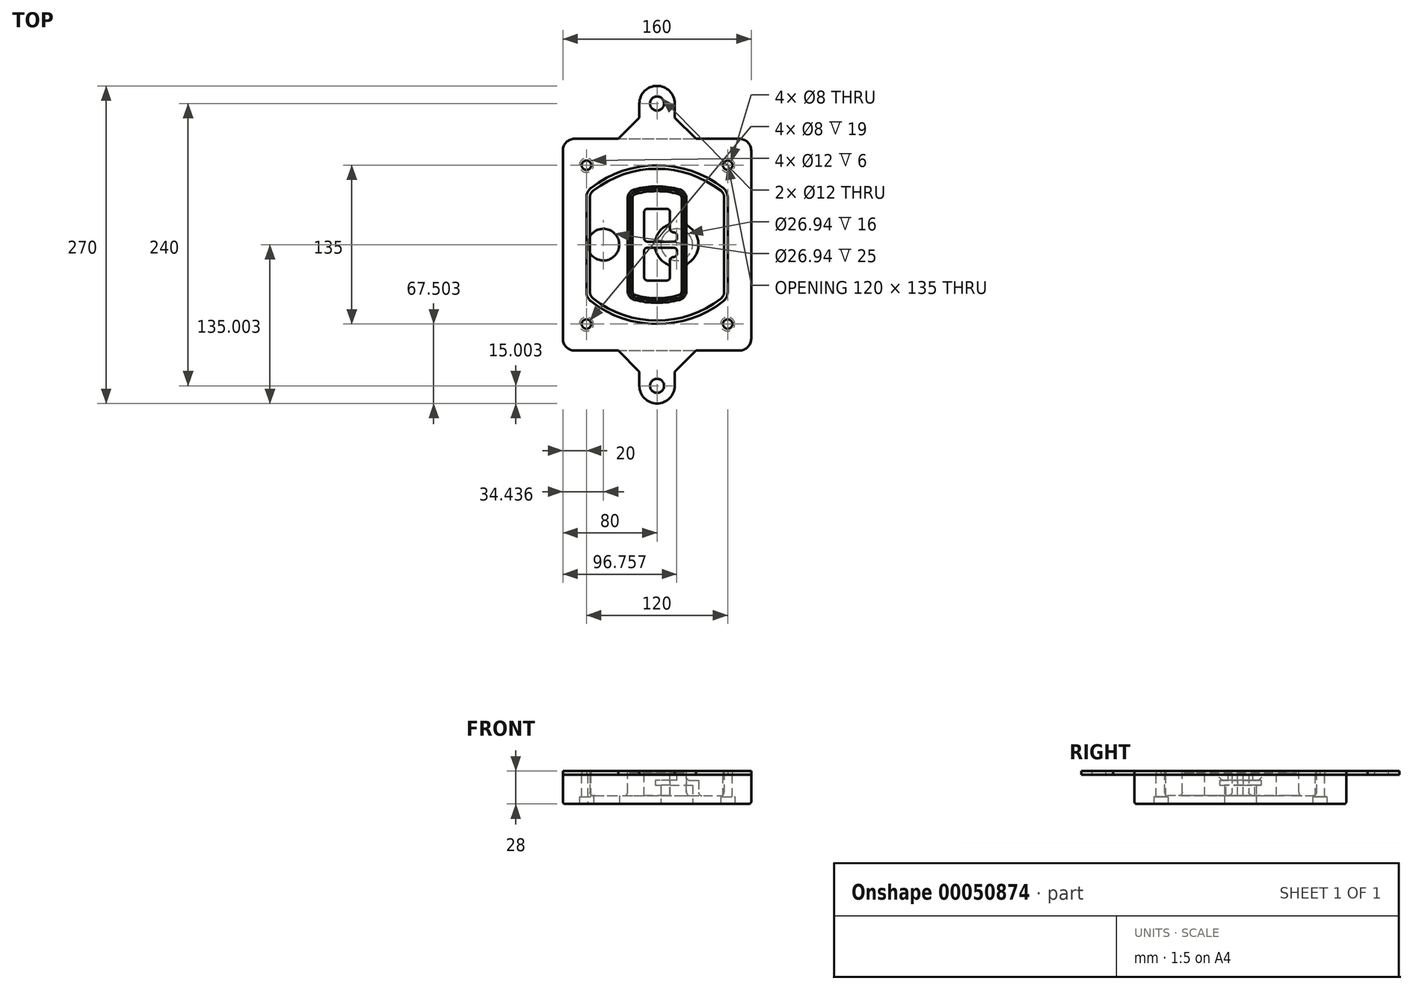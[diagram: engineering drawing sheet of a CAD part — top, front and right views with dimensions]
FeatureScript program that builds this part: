
annotation { "Feature Type Name" : "Feature", "Feature Type Description" : "" }
export const myFeature = defineFeature(function(context is Context, id is Id, definition is map)
    precondition{}
    {
        {
            var Q0;
            Q0=qCreatedBy(makeId("Top.planeOp"),FACE);
            var sketch = newSketch(context, id + "F0", { "sketchPlane" : qUnion([Q0])});
            skPoint(sketch, "E0.rect.middle", {"position": v(0, 0) * mm});
            skLineSegment(sketch, "E1.bottom", {"start": v(24.05, 28.38) * mm, "end": v(164.05, 28.38) * mm});
            skLineSegment(sketch, "E1.top", {"start": v(24.05, 208.38) * mm, "end": v(164.05, 208.38) * mm});
            skLineSegment(sketch, "E1.left", {"start": v(14.05, 38.38) * mm, "end": v(14.05, 198.38) * mm});
            skLineSegment(sketch, "E1.right", {"start": v(174.05, 38.38) * mm, "end": v(174.05, 198.38) * mm});
            skLineSegment(sketch, "E2", {"start": v(14.05, 208.38) * mm, "end": v(174.05, 28.38) * mm, "construction": true});
            skLineSegment(sketch, "E3", {"start": v(174.05, 208.38) * mm, "end": v(14.05, 28.38) * mm, "construction": true});
            skCircle(sketch, "E4", {"center": v(34.05, 185.88) * mm, "radius": 4 * mm});
            skCircle(sketch, "E5", {"center": v(154.05, 185.88) * mm, "radius": 4 * mm});
            skCircle(sketch, "E6", {"center": v(154.05, 50.88) * mm, "radius": 4 * mm});
            skCircle(sketch, "E7", {"center": v(34.05, 50.88) * mm, "radius": 4 * mm});
            skLineSegment(sketch, "E8", {"start": v(34.05, 185.88) * mm, "end": v(154.05, 185.88) * mm, "construction": true});
            skLineSegment(sketch, "E9", {"start": v(154.05, 185.88) * mm, "end": v(154.05, 50.88) * mm, "construction": true});
            skLineSegment(sketch, "E10", {"start": v(154.05, 50.88) * mm, "end": v(34.05, 50.88) * mm, "construction": true});
            skLineSegment(sketch, "E11", {"start": v(34.05, 50.88) * mm, "end": v(34.05, 185.88) * mm, "construction": true});
            skLineSegment(sketch, "E12", {"start": v(34.05, 158.68) * mm, "end": v(34.05, 78.09) * mm});
            skLineSegment(sketch, "E13", {"start": v(154.05, 158.68) * mm, "end": v(154.05, 78.09) * mm});
            skArc(sketch, "E14", {"start": v(150.2, 166.56) * mm, "mid": v(94.05, 185.88) * mm, "end": v(37.9, 166.56) * mm});
            skArc(sketch, "E15", {"start": v(37.9, 70.2) * mm, "mid": v(94.05, 50.88) * mm, "end": v(150.2, 70.2) * mm});
            skLineSegment(sketch, "E16", {"start": v(34.05, 118.38) * mm, "end": v(154.05, 118.38) * mm, "construction": true});
            skPoint(sketch, "E17.visualSharp", {"position": v(34.05, 73.38) * mm});
            skArc(sketch, "E17.filletArc", {"start": v(34.05, 78.09) * mm, "mid": v(35.06, 73.7) * mm, "end": v(37.9, 70.2) * mm});
            skPoint(sketch, "E18.visualSharp", {"position": v(34.05, 163.38) * mm});
            skArc(sketch, "E18.filletArc", {"start": v(37.9, 166.56) * mm, "mid": v(35.06, 163.06) * mm, "end": v(34.05, 158.68) * mm});
            skPoint(sketch, "E19.visualSharp", {"position": v(154.05, 163.38) * mm});
            skArc(sketch, "E19.filletArc", {"start": v(154.05, 158.68) * mm, "mid": v(153.04, 163.06) * mm, "end": v(150.2, 166.56) * mm});
            skPoint(sketch, "E20.visualSharp", {"position": v(154.05, 73.38) * mm});
            skArc(sketch, "E20.filletArc", {"start": v(150.2, 70.2) * mm, "mid": v(153.04, 73.7) * mm, "end": v(154.05, 78.09) * mm});
            skPoint(sketch, "E21.visualSharp", {"position": v(14.05, 208.38) * mm});
            skArc(sketch, "E21.filletArc", {"start": v(24.05, 208.38) * mm, "mid": v(16.98, 205.45) * mm, "end": v(14.05, 198.38) * mm});
            skPoint(sketch, "E22.visualSharp", {"position": v(174.05, 208.38) * mm});
            skArc(sketch, "E22.filletArc", {"start": v(174.05, 198.38) * mm, "mid": v(171.12, 205.45) * mm, "end": v(164.05, 208.38) * mm});
            skPoint(sketch, "E23.visualSharp", {"position": v(174.05, 28.38) * mm});
            skArc(sketch, "E23.filletArc", {"start": v(164.05, 28.38) * mm, "mid": v(171.12, 31.31) * mm, "end": v(174.05, 38.38) * mm});
            skPoint(sketch, "E24.visualSharp", {"position": v(14.05, 28.38) * mm});
            skArc(sketch, "E24.filletArc", {"start": v(14.05, 38.38) * mm, "mid": v(16.98, 31.31) * mm, "end": v(24.05, 28.38) * mm});
            skArc(sketch, "E25.0", {"start": v(151.05, 158.68) * mm, "mid": v(150.34, 161.75) * mm, "end": v(148.36, 164.2) * mm});
            skLineSegment(sketch, "E25.1", {"start": v(151.05, 158.68) * mm, "end": v(151.05, 78.09) * mm});
            skArc(sketch, "E25.2", {"start": v(148.36, 72.57) * mm, "mid": v(150.34, 75.02) * mm, "end": v(151.05, 78.09) * mm});
            skArc(sketch, "E25.3", {"start": v(39.74, 72.57) * mm, "mid": v(94.05, 53.88) * mm, "end": v(148.36, 72.57) * mm});
            skArc(sketch, "E25.4", {"start": v(37.05, 78.09) * mm, "mid": v(37.76, 75.02) * mm, "end": v(39.74, 72.57) * mm});
            skArc(sketch, "E25.5", {"start": v(148.36, 164.2) * mm, "mid": v(94.05, 182.88) * mm, "end": v(39.74, 164.2) * mm});
            skLineSegment(sketch, "E25.6", {"start": v(37.05, 158.68) * mm, "end": v(37.05, 78.09) * mm});
            skArc(sketch, "E25.7", {"start": v(39.74, 164.2) * mm, "mid": v(37.76, 161.75) * mm, "end": v(37.05, 158.68) * mm});
            skArc(sketch, "E26.0", {"start": v(35.43, 169.71) * mm, "mid": v(31.47, 164.82) * mm, "end": v(30.05, 158.68) * mm});
            skArc(sketch, "E26.1", {"start": v(152.67, 169.71) * mm, "mid": v(94.05, 189.88) * mm, "end": v(35.43, 169.71) * mm});
            skArc(sketch, "E26.2", {"start": v(158.05, 158.68) * mm, "mid": v(156.63, 164.82) * mm, "end": v(152.67, 169.71) * mm});
            skLineSegment(sketch, "E26.3", {"start": v(158.05, 158.68) * mm, "end": v(158.05, 78.09) * mm});
            skArc(sketch, "E26.4", {"start": v(152.67, 67.05) * mm, "mid": v(156.63, 71.95) * mm, "end": v(158.05, 78.09) * mm});
            skLineSegment(sketch, "E26.5", {"start": v(30.05, 158.68) * mm, "end": v(30.05, 78.09) * mm});
            skArc(sketch, "E26.6", {"start": v(35.43, 67.05) * mm, "mid": v(94.05, 46.88) * mm, "end": v(152.67, 67.05) * mm});
            skArc(sketch, "E26.7", {"start": v(30.05, 78.09) * mm, "mid": v(31.47, 71.95) * mm, "end": v(35.43, 67.05) * mm});
            skSolve(sketch);
        }
        {
            var Q0;
            Q0=makeQuery(id+"F0.imprint","IMPRINT",FACE,{"disambiguationData":[TD([[makeQuery(id+"F0.imprint","IMPRINT",EDGE,{"derivedFrom":sQuery(id+"F0.wireOp",EDGE,"E1.bottom")}),1.0]])]});
            var Q1;
            Q1=makeQuery(id+"F0.imprint","IMPRINT",FACE,{"disambiguationData":[TD([[makeQuery(id+"F0.imprint","IMPRINT",EDGE,{"derivedFrom":sQuery(id+"F0.wireOp",EDGE,"E12")}),1.0]])]});
            var Q2;
            Q2=makeQuery(id+"F0.imprint","IMPRINT",FACE,{"disambiguationData":[TD([[makeQuery(id+"F0.imprint","IMPRINT",EDGE,{"derivedFrom":sQuery(id+"F0.wireOp",EDGE,"E25.0")}),1.0]])]});
            var Q3;
            Q3=makeQuery(id+"F0.imprint","IMPRINT",FACE,{"disambiguationData":[TD([[makeQuery(id+"F0.imprint","IMPRINT",EDGE,{"derivedFrom":sQuery(id+"F0.wireOp",EDGE,"E12")}),-1.0]])]});
            extrude(context, id + "F1", {"entities" : qUnion([Q0, Q1, Q2, Q3]), "oppositeDirection" : true, "depth" : 25 * mm});
        }
        {
            var Q0;
            Q0=makeQuery(id+"F0.imprint","IMPRINT",FACE,{"disambiguationData":[TD([[makeQuery(id+"F0.imprint","IMPRINT",EDGE,{"derivedFrom":sQuery(id+"F0.wireOp",EDGE,"E12")}),1.0]])]});
            extrude(context, id + "F2", {"entities" : qUnion([Q0]), "operationType" : NewBodyOperationType.ADD, "depth" : 3 * mm});
        }
        {
            var Q0;
            Q0=makeQuery(id+"F0.imprint","IMPRINT",FACE,{"disambiguationData":[TD([[makeQuery(id+"F0.imprint","IMPRINT",EDGE,{"derivedFrom":sQuery(id+"F0.wireOp",EDGE,"E25.0")}),1.0]])]});
            extrude(context, id + "F3", {"entities" : qUnion([Q0]), "operationType" : NewBodyOperationType.REMOVE, "oppositeDirection" : true, "depth" : 18 * mm});
        }
        {
            var Q0;
            Q0=makeQuery(id+"F2.opExtrude","CAP_FACE",FACE,{"disambiguationData":[OSD([sQuery(id+"F0.wireOp",EDGE,"E12"),sQuery(id+"F0.wireOp",EDGE,"E13"),sQuery(id+"F0.wireOp",EDGE,"E14"),sQuery(id+"F0.wireOp",EDGE,"E15"),sQuery(id+"F0.wireOp",EDGE,"E17.filletArc"),sQuery(id+"F0.wireOp",EDGE,"E18.filletArc"),sQuery(id+"F0.wireOp",EDGE,"E19.filletArc"),sQuery(id+"F0.wireOp",EDGE,"E20.filletArc"),sQuery(id+"F0.wireOp",EDGE,"E25.0"),sQuery(id+"F0.wireOp",EDGE,"E25.1"),sQuery(id+"F0.wireOp",EDGE,"E25.2"),sQuery(id+"F0.wireOp",EDGE,"E25.3"),sQuery(id+"F0.wireOp",EDGE,"E25.4"),sQuery(id+"F0.wireOp",EDGE,"E25.5"),sQuery(id+"F0.wireOp",EDGE,"E25.6"),sQuery(id+"F0.wireOp",EDGE,"E25.7")])],"isStart":false});
            var sketch = newSketch(context, id + "F4", { "sketchPlane" : qUnion([Q0])});
            skArc(sketch, "E27.0", {"start": v(74.97, 71.41) * mm, "mid": v(94.05, 68.88) * mm, "end": v(113.13, 71.41) * mm});
            skArc(sketch, "E28.0", {"start": v(113.13, 165.35) * mm, "mid": v(94.05, 167.88) * mm, "end": v(74.97, 165.35) * mm});
            skLineSegment(sketch, "E29", {"start": v(69.05, 157.63) * mm, "end": v(69.05, 79.14) * mm});
            skLineSegment(sketch, "E30", {"start": v(119.05, 157.63) * mm, "end": v(119.05, 79.14) * mm});
            skLineSegment(sketch, "E31", {"start": v(69.05, 163.48) * mm, "end": v(119.05, 163.48) * mm, "construction": true});
            skLineSegment(sketch, "E32", {"start": v(69.05, 73.28) * mm, "end": v(119.05, 73.28) * mm, "construction": true});
            skPoint(sketch, "E33.visualSharp", {"position": v(69.05, 163.48) * mm});
            skArc(sketch, "E33.filletArc", {"start": v(74.97, 165.35) * mm, "mid": v(70.7, 162.5) * mm, "end": v(69.05, 157.63) * mm});
            skPoint(sketch, "E34.visualSharp", {"position": v(119.05, 163.48) * mm});
            skArc(sketch, "E34.filletArc", {"start": v(119.05, 157.63) * mm, "mid": v(117.4, 162.5) * mm, "end": v(113.13, 165.35) * mm});
            skPoint(sketch, "E35.visualSharp", {"position": v(119.05, 73.28) * mm});
            skArc(sketch, "E35.filletArc", {"start": v(113.13, 71.41) * mm, "mid": v(117.4, 74.27) * mm, "end": v(119.05, 79.14) * mm});
            skPoint(sketch, "E36.visualSharp", {"position": v(69.05, 73.28) * mm});
            skArc(sketch, "E36.filletArc", {"start": v(69.05, 79.14) * mm, "mid": v(70.7, 74.27) * mm, "end": v(74.97, 71.41) * mm});
            skArc(sketch, "E37.0", {"start": v(148.36, 164.2) * mm, "mid": v(94.05, 182.88) * mm, "end": v(39.74, 164.2) * mm});
            skArc(sketch, "E37.1", {"start": v(39.74, 164.2) * mm, "mid": v(37.76, 161.75) * mm, "end": v(37.05, 158.68) * mm});
            skLineSegment(sketch, "E37.2", {"start": v(37.05, 158.68) * mm, "end": v(37.05, 78.09) * mm});
            skArc(sketch, "E37.3", {"start": v(37.05, 78.09) * mm, "mid": v(37.76, 75.02) * mm, "end": v(39.74, 72.57) * mm});
            skArc(sketch, "E37.4", {"start": v(39.74, 72.57) * mm, "mid": v(94.05, 53.88) * mm, "end": v(148.36, 72.57) * mm});
            skArc(sketch, "E37.5", {"start": v(148.36, 72.57) * mm, "mid": v(150.34, 75.02) * mm, "end": v(151.05, 78.09) * mm});
            skLineSegment(sketch, "E37.6", {"start": v(151.05, 158.68) * mm, "end": v(151.05, 78.09) * mm});
            skArc(sketch, "E37.7", {"start": v(151.05, 158.68) * mm, "mid": v(150.34, 161.75) * mm, "end": v(148.36, 164.2) * mm});
            skLineSegment(sketch, "E38.0", {"start": v(117.05, 157.63) * mm, "end": v(117.05, 79.14) * mm});
            skArc(sketch, "E38.1", {"start": v(112.61, 73.34) * mm, "mid": v(115.81, 75.49) * mm, "end": v(117.05, 79.14) * mm});
            skArc(sketch, "E38.2", {"start": v(75.49, 73.34) * mm, "mid": v(94.05, 70.88) * mm, "end": v(112.61, 73.34) * mm});
            skArc(sketch, "E38.3", {"start": v(71.05, 79.14) * mm, "mid": v(72.29, 75.49) * mm, "end": v(75.49, 73.34) * mm});
            skLineSegment(sketch, "E38.4", {"start": v(71.05, 157.63) * mm, "end": v(71.05, 79.14) * mm});
            skArc(sketch, "E38.5", {"start": v(117.05, 157.63) * mm, "mid": v(115.81, 161.28) * mm, "end": v(112.61, 163.42) * mm});
            skArc(sketch, "E38.6", {"start": v(75.49, 163.42) * mm, "mid": v(72.29, 161.28) * mm, "end": v(71.05, 157.63) * mm});
            skArc(sketch, "E38.7", {"start": v(112.61, 163.42) * mm, "mid": v(94.05, 165.88) * mm, "end": v(75.49, 163.42) * mm});
            skArc(sketch, "E39.0", {"start": v(115.05, 157.63) * mm, "mid": v(114.23, 160.06) * mm, "end": v(112.1, 161.5) * mm});
            skLineSegment(sketch, "E39.1", {"start": v(115.05, 157.63) * mm, "end": v(115.05, 79.14) * mm});
            skArc(sketch, "E39.2", {"start": v(112.1, 75.27) * mm, "mid": v(114.23, 76.7) * mm, "end": v(115.05, 79.14) * mm});
            skArc(sketch, "E39.3", {"start": v(76, 75.27) * mm, "mid": v(94.05, 72.88) * mm, "end": v(112.1, 75.27) * mm});
            skArc(sketch, "E39.4", {"start": v(73.05, 79.14) * mm, "mid": v(73.87, 76.7) * mm, "end": v(76, 75.27) * mm});
            skArc(sketch, "E39.5", {"start": v(112.1, 161.5) * mm, "mid": v(94.05, 163.88) * mm, "end": v(76, 161.5) * mm});
            skLineSegment(sketch, "E39.6", {"start": v(73.05, 157.63) * mm, "end": v(73.05, 79.14) * mm});
            skArc(sketch, "E39.7", {"start": v(76, 161.5) * mm, "mid": v(73.87, 160.06) * mm, "end": v(73.05, 157.63) * mm});
            skLineSegment(sketch, "E40", {"start": v(69.05, 118.38) * mm, "end": v(119.05, 118.38) * mm, "construction": true});
            skLineSegment(sketch, "E41", {"start": v(83.05, 123.88) * mm, "end": v(83.05, 145.88) * mm});
            skLineSegment(sketch, "E42", {"start": v(86.05, 148.88) * mm, "end": v(102.05, 148.88) * mm});
            skLineSegment(sketch, "E43", {"start": v(105.05, 145.88) * mm, "end": v(105.05, 131.88) * mm});
            skLineSegment(sketch, "E44", {"start": v(108.05, 128.88) * mm, "end": v(108.05, 128.88) * mm});
            skLineSegment(sketch, "E45", {"start": v(111.05, 125.88) * mm, "end": v(111.05, 123.88) * mm});
            skLineSegment(sketch, "E46", {"start": v(108.05, 120.88) * mm, "end": v(86.05, 120.88) * mm});
            skPoint(sketch, "E47.visualSharp", {"position": v(83.05, 148.88) * mm});
            skArc(sketch, "E47.filletArc", {"start": v(86.05, 148.88) * mm, "mid": v(83.93, 148) * mm, "end": v(83.05, 145.88) * mm});
            skPoint(sketch, "E48.visualSharp", {"position": v(105.05, 148.88) * mm});
            skArc(sketch, "E48.filletArc", {"start": v(105.05, 145.88) * mm, "mid": v(104.17, 148) * mm, "end": v(102.05, 148.88) * mm});
            skPoint(sketch, "E49.visualSharp", {"position": v(105.05, 128.88) * mm});
            skArc(sketch, "E49.filletArc", {"start": v(105.05, 131.88) * mm, "mid": v(105.93, 129.76) * mm, "end": v(108.05, 128.88) * mm});
            skPoint(sketch, "E50.visualSharp", {"position": v(111.05, 128.88) * mm});
            skArc(sketch, "E50.filletArc", {"start": v(111.05, 125.88) * mm, "mid": v(110.17, 128) * mm, "end": v(108.05, 128.88) * mm});
            skPoint(sketch, "E51.visualSharp", {"position": v(111.05, 120.88) * mm});
            skArc(sketch, "E51.filletArc", {"start": v(108.05, 120.88) * mm, "mid": v(110.17, 121.76) * mm, "end": v(111.05, 123.88) * mm});
            skPoint(sketch, "E52.visualSharp", {"position": v(83.05, 120.88) * mm});
            skArc(sketch, "E52.filletArc", {"start": v(83.05, 123.88) * mm, "mid": v(83.93, 121.76) * mm, "end": v(86.05, 120.88) * mm});
            skLineSegment(sketch, "E53.0.MirrorCS", {"start": v(108.05, 115.88) * mm, "end": v(86.05, 115.88) * mm});
            skArc(sketch, "E54.0.MirrorCS", {"start": v(83.05, 112.88) * mm, "mid": v(83.93, 115) * mm, "end": v(86.05, 115.88) * mm});
            skLineSegment(sketch, "E55.0.MirrorCS", {"start": v(83.05, 112.88) * mm, "end": v(83.05, 90.88) * mm});
            skArc(sketch, "E56.0.MirrorCS", {"start": v(86.05, 87.88) * mm, "mid": v(83.93, 88.76) * mm, "end": v(83.05, 90.88) * mm});
            skLineSegment(sketch, "E57.0.MirrorCS", {"start": v(86.05, 87.88) * mm, "end": v(102.05, 87.88) * mm});
            skArc(sketch, "E58.0.MirrorCS", {"start": v(105.05, 90.88) * mm, "mid": v(104.17, 88.76) * mm, "end": v(102.05, 87.88) * mm});
            skLineSegment(sketch, "E59.0.MirrorCS", {"start": v(105.05, 90.88) * mm, "end": v(105.05, 104.88) * mm});
            skArc(sketch, "E60.0.MirrorCS", {"start": v(105.05, 104.88) * mm, "mid": v(105.93, 107) * mm, "end": v(108.05, 107.88) * mm});
            skArc(sketch, "E61.0.MirrorCS", {"start": v(111.05, 110.88) * mm, "mid": v(110.17, 108.76) * mm, "end": v(108.05, 107.88) * mm});
            skLineSegment(sketch, "E62.0.MirrorCS", {"start": v(111.05, 110.88) * mm, "end": v(111.05, 112.88) * mm});
            skArc(sketch, "E63.0.MirrorCS", {"start": v(108.05, 115.88) * mm, "mid": v(110.17, 115) * mm, "end": v(111.05, 112.88) * mm});
            skSolve(sketch);
        }
        {
            var Q0;
            Q0=makeQuery(id+"F4.imprint","IMPRINT",FACE,{"disambiguationData":[TD([[makeQuery(id+"F4.imprint","IMPRINT",EDGE,{"derivedFrom":sQuery(id+"F4.wireOp",EDGE,"E27.0")}),1.0]])]});
            var Q1;
            Q1=makeQuery(id+"F4.imprint","IMPRINT",FACE,{"disambiguationData":[TD([[makeQuery(id+"F4.imprint","IMPRINT",EDGE,{"derivedFrom":sQuery(id+"F4.wireOp",EDGE,"E38.0")}),-1.0]])]});
            var Q2;
            Q2=makeQuery(id+"F4.imprint","IMPRINT",FACE,{"disambiguationData":[TD([[makeQuery(id+"F4.imprint","IMPRINT",EDGE,{"derivedFrom":sQuery(id+"F4.wireOp",EDGE,"E39.0")}),1.0]])]});
            extrude(context, id + "F5", {"entities" : qUnion([Q0, Q1, Q2]), "operationType" : NewBodyOperationType.ADD, "endBound" : BoundingType.UP_TO_NEXT, "oppositeDirection" : true, "depth" : 25 * mm});
        }
        {
            var Q0;
            Q0=makeQuery(id+"F4.imprint","IMPRINT",FACE,{"disambiguationData":[TD([[makeQuery(id+"F4.imprint","IMPRINT",EDGE,{"derivedFrom":sQuery(id+"F4.wireOp",EDGE,"E38.0")}),-1.0]])]});
            extrude(context, id + "F6", {"entities" : qUnion([Q0]), "operationType" : NewBodyOperationType.REMOVE, "oppositeDirection" : true, "depth" : 2 * mm});
        }
        {
            var Q0;
            Q0=makeQuery(id+"F1.opExtrude","CAP_FACE",FACE,{"disambiguationData":[OSD([sQuery(id+"F0.wireOp",EDGE,"E1.bottom"),sQuery(id+"F0.wireOp",EDGE,"E1.top"),sQuery(id+"F0.wireOp",EDGE,"E1.left"),sQuery(id+"F0.wireOp",EDGE,"E1.right"),sQuery(id+"F0.wireOp",EDGE,"E4"),sQuery(id+"F0.wireOp",EDGE,"E5"),sQuery(id+"F0.wireOp",EDGE,"E6"),sQuery(id+"F0.wireOp",EDGE,"E7"),sQuery(id+"F0.wireOp",EDGE,"E21.filletArc"),sQuery(id+"F0.wireOp",EDGE,"E22.filletArc"),sQuery(id+"F0.wireOp",EDGE,"E23.filletArc"),sQuery(id+"F0.wireOp",EDGE,"E24.filletArc")])],"isStart":false});
            var sketch = newSketch(context, id + "F7", { "sketchPlane" : qUnion([Q0])});
            skCircle(sketch, "E64", {"center": v(110.8, -118.38) * mm, "radius": 13.47 * mm});
            skCircle(sketch, "E65", {"center": v(48.49, -118.38) * mm, "radius": 13.47 * mm});
            skLineSegment(sketch, "E66", {"start": v(174.05, -118.38) * mm, "end": v(14.05, -118.38) * mm});
            skCircle(sketch, "E67", {"center": v(110.8, -118.38) * mm, "radius": 18.47 * mm});
            skCircle(sketch, "E68", {"center": v(154.05, -185.88) * mm, "radius": 6 * mm});
            skCircle(sketch, "E69", {"center": v(34.05, -185.88) * mm, "radius": 6 * mm});
            skCircle(sketch, "E70", {"center": v(34.05, -50.88) * mm, "radius": 6 * mm});
            skCircle(sketch, "E71", {"center": v(154.05, -50.88) * mm, "radius": 6 * mm});
            skSolve(sketch);
        }
        {
            var Q0;
            {var subQ1=sQuery(id+"F7.wireOp",EDGE,"E66");var subQ4=sQuery(id+"F7.wireOp",EDGE,"E64");var subQ6=makeQuery(id+"F7.imprint","INTERSECT",VERTEX,{"disambiguationData":[OD(0.0)],"derivedFrom":[subQ4,subQ1]});Q0=makeQuery(id+"F7.imprint","IMPRINT",FACE,{"disambiguationData":[TD([[makeQuery(id+"F7.imprint","IMPRINT",EDGE,{"disambiguationData":[TD([[subQ6,-1.0]])],"derivedFrom":subQ4}),-1.0]])]});}
            var Q1;
            {var subQ0=sQuery(id+"F7.wireOp",EDGE,"E66");var subQ1=sQuery(id+"F7.wireOp",EDGE,"E64");var subQ3=makeQuery(id+"F7.imprint","INTERSECT",VERTEX,{"disambiguationData":[OD(0.0)],"derivedFrom":[subQ1,subQ0]});Q1=makeQuery(id+"F7.imprint","IMPRINT",FACE,{"disambiguationData":[TD([[makeQuery(id+"F7.imprint","IMPRINT",EDGE,{"disambiguationData":[TD([[subQ3,-1.0]])],"derivedFrom":subQ1}),1.0]])]});}
            var Q2;
            {var subQ0=sQuery(id+"F7.wireOp",EDGE,"E66");var subQ1=sQuery(id+"F7.wireOp",EDGE,"E64");var subQ3=makeQuery(id+"F7.imprint","INTERSECT",VERTEX,{"disambiguationData":[OD(0.0)],"derivedFrom":[subQ1,subQ0]});Q2=makeQuery(id+"F7.imprint","IMPRINT",FACE,{"disambiguationData":[TD([[makeQuery(id+"F7.imprint","IMPRINT",EDGE,{"disambiguationData":[TD([[subQ3,1.0]])],"derivedFrom":subQ1}),1.0]])]});}
            var Q3;
            {var subQ1=sQuery(id+"F7.wireOp",EDGE,"E66");var subQ4=sQuery(id+"F7.wireOp",EDGE,"E64");var subQ6=makeQuery(id+"F7.imprint","INTERSECT",VERTEX,{"disambiguationData":[OD(0.0)],"derivedFrom":[subQ4,subQ1]});Q3=makeQuery(id+"F7.imprint","IMPRINT",FACE,{"disambiguationData":[TD([[makeQuery(id+"F7.imprint","IMPRINT",EDGE,{"disambiguationData":[TD([[subQ6,1.0]])],"derivedFrom":subQ4}),-1.0]])]});}
            extrude(context, id + "F8", {"entities" : qUnion([Q0, Q1, Q2, Q3]), "operationType" : NewBodyOperationType.ADD, "oppositeDirection" : true, "depth" : 20 * mm});
        }
        {
            var Q0;
            {var subQ0=sQuery(id+"F7.wireOp",EDGE,"E66");var subQ1=sQuery(id+"F7.wireOp",EDGE,"E64");var subQ3=makeQuery(id+"F7.imprint","INTERSECT",VERTEX,{"disambiguationData":[OD(0.0)],"derivedFrom":[subQ1,subQ0]});Q0=makeQuery(id+"F7.imprint","IMPRINT",FACE,{"disambiguationData":[TD([[makeQuery(id+"F7.imprint","IMPRINT",EDGE,{"disambiguationData":[TD([[subQ3,-1.0]])],"derivedFrom":subQ1}),1.0]])]});}
            var Q1;
            {var subQ0=sQuery(id+"F7.wireOp",EDGE,"E66");var subQ1=sQuery(id+"F7.wireOp",EDGE,"E64");var subQ3=makeQuery(id+"F7.imprint","INTERSECT",VERTEX,{"disambiguationData":[OD(0.0)],"derivedFrom":[subQ1,subQ0]});Q1=makeQuery(id+"F7.imprint","IMPRINT",FACE,{"disambiguationData":[TD([[makeQuery(id+"F7.imprint","IMPRINT",EDGE,{"disambiguationData":[TD([[subQ3,1.0]])],"derivedFrom":subQ1}),1.0]])]});}
            extrude(context, id + "F9", {"entities" : qUnion([Q0, Q1]), "operationType" : NewBodyOperationType.REMOVE, "oppositeDirection" : true, "depth" : 16 * mm});
        }
        {
            var Q0;
            {var subQ0=sQuery(id+"F7.wireOp",EDGE,"E66");var subQ1=sQuery(id+"F7.wireOp",EDGE,"E65");var subQ3=makeQuery(id+"F7.imprint","INTERSECT",VERTEX,{"disambiguationData":[OD(0.0)],"derivedFrom":[subQ1,subQ0]});Q0=makeQuery(id+"F7.imprint","IMPRINT",FACE,{"disambiguationData":[TD([[makeQuery(id+"F7.imprint","IMPRINT",EDGE,{"disambiguationData":[TD([[subQ3,-1.0]])],"derivedFrom":subQ1}),1.0]])]});}
            var Q1;
            {var subQ0=sQuery(id+"F7.wireOp",EDGE,"E66");var subQ1=sQuery(id+"F7.wireOp",EDGE,"E65");var subQ3=makeQuery(id+"F7.imprint","INTERSECT",VERTEX,{"disambiguationData":[OD(0.0)],"derivedFrom":[subQ1,subQ0]});Q1=makeQuery(id+"F7.imprint","IMPRINT",FACE,{"disambiguationData":[TD([[makeQuery(id+"F7.imprint","IMPRINT",EDGE,{"disambiguationData":[TD([[subQ3,1.0]])],"derivedFrom":subQ1}),1.0]])]});}
            extrude(context, id + "F10", {"entities" : qUnion([Q0, Q1]), "operationType" : NewBodyOperationType.REMOVE, "oppositeDirection" : true, "depth" : 25 * mm});
        }
        {
            var Q0;
            Q0=makeQuery(id+"F7.imprint","IMPRINT",FACE,{"disambiguationData":[TD([[makeQuery(id+"F7.imprint","IMPRINT",EDGE,{"derivedFrom":sQuery(id+"F7.wireOp",EDGE,"E68")}),1.0]])]});
            var Q1;
            Q1=makeQuery(id+"F7.imprint","IMPRINT",FACE,{"disambiguationData":[TD([[makeQuery(id+"F7.imprint","IMPRINT",EDGE,{"derivedFrom":makeQuery(id+"F1.opExtrude","CAP_EDGE",EDGE,{"disambiguationData":[OSD([sQuery(id+"F0.wireOp",EDGE,"E5")])],"isStart":false})}),-1.0]])]});
            var Q2;
            Q2=makeQuery(id+"F7.imprint","IMPRINT",FACE,{"disambiguationData":[TD([[makeQuery(id+"F7.imprint","IMPRINT",EDGE,{"derivedFrom":sQuery(id+"F7.wireOp",EDGE,"E69")}),1.0]])]});
            var Q3;
            Q3=makeQuery(id+"F7.imprint","IMPRINT",FACE,{"disambiguationData":[TD([[makeQuery(id+"F7.imprint","IMPRINT",EDGE,{"derivedFrom":makeQuery(id+"F1.opExtrude","CAP_EDGE",EDGE,{"disambiguationData":[OSD([sQuery(id+"F0.wireOp",EDGE,"E4")])],"isStart":false})}),-1.0]])]});
            var Q4;
            Q4=makeQuery(id+"F7.imprint","IMPRINT",FACE,{"disambiguationData":[TD([[makeQuery(id+"F7.imprint","IMPRINT",EDGE,{"derivedFrom":sQuery(id+"F7.wireOp",EDGE,"E70")}),1.0]])]});
            var Q5;
            Q5=makeQuery(id+"F7.imprint","IMPRINT",FACE,{"disambiguationData":[TD([[makeQuery(id+"F7.imprint","IMPRINT",EDGE,{"derivedFrom":makeQuery(id+"F1.opExtrude","CAP_EDGE",EDGE,{"disambiguationData":[OSD([sQuery(id+"F0.wireOp",EDGE,"E7")])],"isStart":false})}),-1.0]])]});
            var Q6;
            Q6=makeQuery(id+"F7.imprint","IMPRINT",FACE,{"disambiguationData":[TD([[makeQuery(id+"F7.imprint","IMPRINT",EDGE,{"derivedFrom":sQuery(id+"F7.wireOp",EDGE,"E71")}),1.0]])]});
            var Q7;
            Q7=makeQuery(id+"F7.imprint","IMPRINT",FACE,{"disambiguationData":[TD([[makeQuery(id+"F7.imprint","IMPRINT",EDGE,{"derivedFrom":makeQuery(id+"F1.opExtrude","CAP_EDGE",EDGE,{"disambiguationData":[OSD([sQuery(id+"F0.wireOp",EDGE,"E6")])],"isStart":false})}),-1.0]])]});
            extrude(context, id + "F11", {"entities" : qUnion([Q0, Q1, Q2, Q3, Q4, Q5, Q6, Q7]), "operationType" : NewBodyOperationType.REMOVE, "oppositeDirection" : true, "depth" : 6 * mm});
        }
        {
            var Q0;
            Q0=makeQuery(id+"F9.boolean.opBoolean","COPY",FACE,{"derivedFrom":makeQuery(id+"F9.opExtrude","CAP_FACE",FACE,{"disambiguationData":[OSD([sQuery(id+"F7.wireOp",EDGE,"E64")])],"isStart":false})});
            var sketch = newSketch(context, id + "F12", { "sketchPlane" : qUnion([Q0])});
            skArc(sketch, "E72.0", {"start": v(105.05, -100.83) * mm, "mid": v(96.62, -106.56) * mm, "end": v(92.5, -115.88) * mm});
            skArc(sketch, "E72.1", {"start": v(92.5, -120.88) * mm, "mid": v(96.62, -130.2) * mm, "end": v(105.05, -135.93) * mm});
            skLineSegment(sketch, "E73", {"start": v(92.5, -120.88) * mm, "end": v(108.05, -120.88) * mm});
            skLineSegment(sketch, "E74.0", {"start": v(108.05, -115.88) * mm, "end": v(92.5, -115.88) * mm});
            skArc(sketch, "E74.1", {"start": v(108.05, -115.88) * mm, "mid": v(110.17, -115) * mm, "end": v(111.05, -112.88) * mm});
            skLineSegment(sketch, "E74.2", {"start": v(111.05, -110.88) * mm, "end": v(111.05, -112.88) * mm});
            skArc(sketch, "E74.3", {"start": v(111.05, -110.88) * mm, "mid": v(110.17, -108.76) * mm, "end": v(108.05, -107.88) * mm});
            skArc(sketch, "E74.4", {"start": v(105.05, -104.88) * mm, "mid": v(105.93, -107) * mm, "end": v(108.05, -107.88) * mm});
            skLineSegment(sketch, "E74.5", {"start": v(105.05, -100.83) * mm, "end": v(105.05, -104.88) * mm});
            skLineSegment(sketch, "E74.7", {"start": v(108.05, -120.88) * mm, "end": v(92.5, -120.88) * mm});
            skArc(sketch, "E74.8", {"start": v(108.05, -120.88) * mm, "mid": v(110.17, -121.76) * mm, "end": v(111.05, -123.88) * mm});
            skLineSegment(sketch, "E74.9", {"start": v(111.05, -125.88) * mm, "end": v(111.05, -123.88) * mm});
            skArc(sketch, "E74.10", {"start": v(111.05, -125.88) * mm, "mid": v(110.17, -128) * mm, "end": v(108.05, -128.88) * mm});
            skArc(sketch, "E74.11", {"start": v(105.05, -131.88) * mm, "mid": v(105.93, -129.76) * mm, "end": v(108.05, -128.88) * mm});
            skLineSegment(sketch, "E74.12", {"start": v(105.05, -135.93) * mm, "end": v(105.05, -131.88) * mm});
            skPoint(sketch, "E75.orphan", {"position": v(105.05, -145.88) * mm});
            skPoint(sketch, "E76.orphan", {"position": v(86.05, -120.88) * mm});
            skPoint(sketch, "E77.orphan", {"position": v(86.05, -115.88) * mm});
            skPoint(sketch, "E78.orphan", {"position": v(105.05, -90.88) * mm});
            skSolve(sketch);
        }
        {
            var Q0;
            {var subQ7=sQuery(id+"F12.wireOp",EDGE,"E72.0");var subQ14=sQuery(id+"F12.wireOp",EDGE,"E72.1");var subQ16=sQuery(id+"F12.wireOp",EDGE,"E74.1");var subQ18=sQuery(id+"F12.wireOp",EDGE,"E74.8");Q0=qUnion([makeQuery(id+"F12.imprint","IMPRINT",FACE,{"disambiguationData":[TD([[makeQuery(id+"F12.imprint","IMPRINT",EDGE,{"derivedFrom":subQ7}),1.0]])]}),makeQuery(id+"F12.imprint","IMPRINT",FACE,{"disambiguationData":[TD([[makeQuery(id+"F12.imprint","IMPRINT",EDGE,{"derivedFrom":subQ14}),1.0]])]}),makeQuery(id+"F12.imprint","IMPRINT",FACE,{"disambiguationData":[TD([[makeQuery(id+"F12.imprint","IMPRINT",EDGE,{"derivedFrom":subQ16}),1.0]])]}),makeQuery(id+"F12.imprint","IMPRINT",FACE,{"disambiguationData":[TD([[makeQuery(id+"F12.imprint","IMPRINT",EDGE,{"derivedFrom":subQ18}),-1.0]])]})]);}
            var Q1;
            Q1=makeQuery(id+"F5.boolean.opBoolean","SPLIT",FACE,{"disambiguationData":[TD([makeQuery(id+"F5.opExtrude","SWEPT_FACE",FACE,{"disambiguationData":[OSD([sQuery(id+"F4.wireOp",EDGE,"E41")])]})])],"derivedFrom":makeQuery(id+"F3.boolean.opBoolean","COPY",FACE,{"derivedFrom":makeQuery(id+"F3.opExtrude","CAP_FACE",FACE,{"disambiguationData":[OSD([sQuery(id+"F0.wireOp",EDGE,"E25.0"),sQuery(id+"F0.wireOp",EDGE,"E25.1"),sQuery(id+"F0.wireOp",EDGE,"E25.2"),sQuery(id+"F0.wireOp",EDGE,"E25.3"),sQuery(id+"F0.wireOp",EDGE,"E25.4"),sQuery(id+"F0.wireOp",EDGE,"E25.5"),sQuery(id+"F0.wireOp",EDGE,"E25.6"),sQuery(id+"F0.wireOp",EDGE,"E25.7")])],"isStart":false})})});
            extrude(context, id + "F13", {"entities" : qUnion([Q0]), "operationType" : NewBodyOperationType.REMOVE, "endBound" : BoundingType.UP_TO_SURFACE, "endBoundEntityFace" : qUnion([Q1]), "depth" : 25 * mm});
        }
        {
            var Q0;
            Q0=makeQuery(id+"F3.boolean.opBoolean","COPY",EDGE,{"derivedFrom":makeQuery(id+"F3.opExtrude","CAP_EDGE",EDGE,{"disambiguationData":[OSD([sQuery(id+"F0.wireOp",EDGE,"E25.6")])],"isStart":false})});
            var Q1;
            Q1=makeQuery(id+"F8.boolean.opBoolean","INTERSECT",EDGE,{"derivedFrom":[makeQuery(id+"F5.opExtrude","SWEPT_FACE",FACE,{"disambiguationData":[OSD([sQuery(id+"F4.wireOp",EDGE,"E30")])]}),makeQuery(id+"F8.opExtrude","CAP_FACE",FACE,{"disambiguationData":[OSD([sQuery(id+"F7.wireOp",EDGE,"E67")])],"isStart":false})]});
            var Q2;
            Q2=makeQuery(id+"F8.boolean.opBoolean","INTERSECT",EDGE,{"disambiguationData":[OD(1.0)],"derivedFrom":[makeQuery(id+"F5.opExtrude","SWEPT_FACE",FACE,{"disambiguationData":[OSD([sQuery(id+"F4.wireOp",EDGE,"E30")])]}),makeQuery(id+"F8.opExtrude","SWEPT_FACE",FACE,{"disambiguationData":[OSD([sQuery(id+"F7.wireOp",EDGE,"E67")])]})]});
            var Q3;
            {var subQ0=sQuery(id+"F4.wireOp",EDGE,"E30");Q3=makeQuery(id+"F8.boolean.opBoolean","SPLIT",EDGE,{"disambiguationData":[TD([makeQuery(id+"F5.opExtrude","SWEPT_FACE",FACE,{"disambiguationData":[OSD([sQuery(id+"F4.wireOp",EDGE,"E35.filletArc")])]})])],"derivedFrom":makeQuery(id+"F5.opExtrude","CAP_EDGE",EDGE,{"disambiguationData":[OSD([subQ0])],"isStart":false})});}
            var Q4;
            {var subQ0=sQuery(id+"F0.wireOp",EDGE,"E25.7");var subQ1=sQuery(id+"F0.wireOp",EDGE,"E25.1");var subQ2=sQuery(id+"F0.wireOp",EDGE,"E25.6");var subQ3=sQuery(id+"F0.wireOp",EDGE,"E25.5");var subQ4=sQuery(id+"F0.wireOp",EDGE,"E25.4");var subQ5=sQuery(id+"F0.wireOp",EDGE,"E25.0");var subQ6=sQuery(id+"F0.wireOp",EDGE,"E25.2");var subQ7=sQuery(id+"F0.wireOp",EDGE,"E25.3");Q4=makeQuery(id+"F8.boolean.opBoolean","INTERSECT",EDGE,{"derivedFrom":[makeQuery(id+"F5.boolean.opBoolean","SPLIT",FACE,{"disambiguationData":[TD([makeQuery(id+"F2.opExtrude","SWEPT_FACE",FACE,{"disambiguationData":[OSD([subQ5])]})])],"derivedFrom":makeQuery(id+"F3.boolean.opBoolean","COPY",FACE,{"derivedFrom":makeQuery(id+"F3.opExtrude","CAP_FACE",FACE,{"disambiguationData":[OSD([subQ5,subQ1,subQ6,subQ7,subQ4,subQ3,subQ2,subQ0])],"isStart":false})})}),makeQuery(id+"F8.opExtrude","SWEPT_FACE",FACE,{"disambiguationData":[OSD([sQuery(id+"F7.wireOp",EDGE,"E67")])]})]});}
            var Q5;
            Q5=makeQuery(id+"F8.boolean.opBoolean","INTERSECT",EDGE,{"disambiguationData":[OD(0.0)],"derivedFrom":[makeQuery(id+"F5.opExtrude","SWEPT_FACE",FACE,{"disambiguationData":[OSD([sQuery(id+"F4.wireOp",EDGE,"E30")])]}),makeQuery(id+"F8.opExtrude","SWEPT_FACE",FACE,{"disambiguationData":[OSD([sQuery(id+"F7.wireOp",EDGE,"E67")])]})]});
            fillet(context, id + "F14", {"entities" : qUnion([Q0, Q1, Q2, Q3, Q4, Q5]), "radius" : 3 * mm, "tangentPropagation" : true, "allowEdgeOverflow" : false});
        }
        {
            var Q0;
            Q0=makeQuery(id+"F1.opExtrude","CAP_EDGE",EDGE,{"disambiguationData":[OSD([sQuery(id+"F0.wireOp",EDGE,"E1.bottom")])],"isStart":false});
            fillet(context, id + "F15", {"entities" : qUnion([Q0]), "radius" : 2 * mm, "tangentPropagation" : true, "allowEdgeOverflow" : false});
        }
        {
            var Q0;
            {var subQ0=sQuery(id+"F0.wireOp",EDGE,"E22.filletArc");var subQ1=sQuery(id+"F0.wireOp",EDGE,"E7");var subQ2=sQuery(id+"F0.wireOp",EDGE,"E6");var subQ3=sQuery(id+"F0.wireOp",EDGE,"E5");var subQ4=sQuery(id+"F0.wireOp",EDGE,"E4");var subQ5=sQuery(id+"F0.wireOp",EDGE,"E1.bottom");var subQ6=sQuery(id+"F0.wireOp",EDGE,"E21.filletArc");var subQ7=sQuery(id+"F0.wireOp",EDGE,"E1.top");var subQ8=sQuery(id+"F0.wireOp",EDGE,"E1.left");var subQ9=sQuery(id+"F0.wireOp",EDGE,"E1.right");var subQ10=sQuery(id+"F0.wireOp",EDGE,"E23.filletArc");var subQ11=sQuery(id+"F0.wireOp",EDGE,"E24.filletArc");Q0=makeQuery(id+"F2.boolean.opBoolean","SPLIT",FACE,{"disambiguationData":[TD([makeQuery(id+"F1.opExtrude","SWEPT_FACE",FACE,{"disambiguationData":[OSD([subQ5])]})])],"derivedFrom":makeQuery(id+"F1.opExtrude","CAP_FACE",FACE,{"disambiguationData":[OSD([subQ5,subQ7,subQ8,subQ9,subQ4,subQ3,subQ2,subQ1,subQ6,subQ0,subQ10,subQ11])],"isStart":true})});}
            var sketch = newSketch(context, id + "F16", { "sketchPlane" : qUnion([Q0])});
            skLineSegment(sketch, "E79", {"start": v(94.05, 208.38) * mm, "end": v(94.05, 238.38) * mm, "construction": true});
            skCircle(sketch, "E80", {"center": v(94.05, 238.38) * mm, "radius": 6 * mm, "construction": true});
            skArc(sketch, "E81", {"start": v(109.05, 238.38) * mm, "mid": v(94.05, 253.38) * mm, "end": v(79.05, 238.38) * mm});
            skLineSegment(sketch, "E82", {"start": v(79.05, 238.38) * mm, "end": v(79.05, 226.38) * mm});
            skLineSegment(sketch, "E83", {"start": v(79.05, 226.38) * mm, "end": v(61.05, 208.38) * mm});
            skLineSegment(sketch, "E84", {"start": v(109.05, 238.38) * mm, "end": v(109.05, 226.38) * mm});
            skLineSegment(sketch, "E85", {"start": v(109.05, 226.38) * mm, "end": v(127.05, 208.38) * mm});
            skLineSegment(sketch, "E86", {"start": v(61.05, 208.38) * mm, "end": v(127.05, 208.38) * mm});
            skLineSegment(sketch, "E87", {"start": v(14.05, 118.38) * mm, "end": v(174.05, 118.38) * mm, "construction": true});
            skLineSegment(sketch, "E88.MirrorCS", {"start": v(79.05, 10.38) * mm, "end": v(61.05, 28.38) * mm});
            skLineSegment(sketch, "E89.MirrorCS", {"start": v(79.05, -1.62) * mm, "end": v(79.05, 10.38) * mm});
            skArc(sketch, "E90.MirrorCS", {"start": v(109.05, -1.62) * mm, "mid": v(94.05, -16.62) * mm, "end": v(79.05, -1.62) * mm});
            skCircle(sketch, "E91.MirrorC", {"center": v(94.05, -1.62) * mm, "radius": 6 * mm, "construction": true});
            skLineSegment(sketch, "E92.MirrorCS", {"start": v(109.05, -1.62) * mm, "end": v(109.05, 10.38) * mm});
            skLineSegment(sketch, "E93.MirrorCS", {"start": v(109.05, 10.38) * mm, "end": v(127.05, 28.38) * mm});
            skLineSegment(sketch, "E94.MirrorCS", {"start": v(61.05, 28.38) * mm, "end": v(127.05, 28.38) * mm});
            skLineSegment(sketch, "E95.MirrorCS", {"start": v(94.05, 28.38) * mm, "end": v(94.05, -1.62) * mm, "construction": true});
            skSolve(sketch);
        }
        {
            var Q0;
            Q0=makeQuery(id+"F16.imprint","IMPRINT",FACE,{"disambiguationData":[TD([[makeQuery(id+"F16.imprint","IMPRINT",EDGE,{"derivedFrom":sQuery(id+"F16.wireOp",EDGE,"E81")}),1.0]])]});
            var Q1;
            {var subQ5=sQuery(id+"F16.wireOp",EDGE,"E86");Q1=makeQuery(id+"F16.imprint","IMPRINT",FACE,{"disambiguationData":[TD([[makeQuery(id+"F16.imprint","IMPRINT",EDGE,{"derivedFrom":subQ5}),-1.0]])]});}
            var Q2;
            Q2=makeQuery(id+"F16.imprint","IMPRINT",FACE,{"disambiguationData":[TD([[makeQuery(id+"F16.imprint","IMPRINT",EDGE,{"derivedFrom":sQuery(id+"F16.wireOp",EDGE,"E88.MirrorCS")}),-1.0]])]});
            var Q3;
            Q3=makeQuery(id+"F2.opExtrude","CAP_FACE",FACE,{"disambiguationData":[OSD([sQuery(id+"F0.wireOp",EDGE,"E12"),sQuery(id+"F0.wireOp",EDGE,"E13"),sQuery(id+"F0.wireOp",EDGE,"E14"),sQuery(id+"F0.wireOp",EDGE,"E15"),sQuery(id+"F0.wireOp",EDGE,"E17.filletArc"),sQuery(id+"F0.wireOp",EDGE,"E18.filletArc"),sQuery(id+"F0.wireOp",EDGE,"E19.filletArc"),sQuery(id+"F0.wireOp",EDGE,"E20.filletArc"),sQuery(id+"F0.wireOp",EDGE,"E25.0"),sQuery(id+"F0.wireOp",EDGE,"E25.1"),sQuery(id+"F0.wireOp",EDGE,"E25.2"),sQuery(id+"F0.wireOp",EDGE,"E25.3"),sQuery(id+"F0.wireOp",EDGE,"E25.4"),sQuery(id+"F0.wireOp",EDGE,"E25.5"),sQuery(id+"F0.wireOp",EDGE,"E25.6"),sQuery(id+"F0.wireOp",EDGE,"E25.7")])],"isStart":false});
            extrude(context, id + "F17", {"entities" : qUnion([Q0, Q1, Q2]), "endBound" : BoundingType.UP_TO_SURFACE, "endBoundEntityFace" : qUnion([Q3]), "depth" : 25 * mm});
        }
        {
            var Q0;
            Q0=makeQuery(id+"F17.opExtrude","CAP_FACE",FACE,{"disambiguationData":[OSD([sQuery(id+"F0.wireOp",EDGE,"E1.bottom"),sQuery(id+"F0.wireOp",EDGE,"E1.top"),sQuery(id+"F0.wireOp",EDGE,"E1.left"),sQuery(id+"F0.wireOp",EDGE,"E1.right"),sQuery(id+"F0.wireOp",EDGE,"E4"),sQuery(id+"F0.wireOp",EDGE,"E5"),sQuery(id+"F0.wireOp",EDGE,"E6"),sQuery(id+"F0.wireOp",EDGE,"E7"),sQuery(id+"F0.wireOp",EDGE,"E12"),sQuery(id+"F0.wireOp",EDGE,"E13"),sQuery(id+"F0.wireOp",EDGE,"E14"),sQuery(id+"F0.wireOp",EDGE,"E15"),sQuery(id+"F0.wireOp",EDGE,"E17.filletArc"),sQuery(id+"F0.wireOp",EDGE,"E18.filletArc"),sQuery(id+"F0.wireOp",EDGE,"E19.filletArc"),sQuery(id+"F0.wireOp",EDGE,"E20.filletArc"),sQuery(id+"F0.wireOp",EDGE,"E21.filletArc"),sQuery(id+"F0.wireOp",EDGE,"E22.filletArc"),sQuery(id+"F0.wireOp",EDGE,"E23.filletArc"),sQuery(id+"F0.wireOp",EDGE,"E24.filletArc"),sQuery(id+"F16.wireOp",EDGE,"E81"),sQuery(id+"F16.wireOp",EDGE,"E82"),sQuery(id+"F16.wireOp",EDGE,"E83"),sQuery(id+"F16.wireOp",EDGE,"E84"),sQuery(id+"F16.wireOp",EDGE,"E85"),sQuery(id+"F16.wireOp",EDGE,"E88.MirrorCS"),sQuery(id+"F16.wireOp",EDGE,"E89.MirrorCS"),sQuery(id+"F16.wireOp",EDGE,"E90.MirrorCS"),sQuery(id+"F16.wireOp",EDGE,"E92.MirrorCS"),sQuery(id+"F16.wireOp",EDGE,"E93.MirrorCS")])],"isStart":false});
            var sketch = newSketch(context, id + "F18", { "sketchPlane" : qUnion([Q0])});
            skCircle(sketch, "E96", {"center": v(94.05, 238.38) * mm, "radius": 6 * mm});
            skCircle(sketch, "E97", {"center": v(94.05, -1.62) * mm, "radius": 6 * mm});
            skSolve(sketch);
        }
        {
            var Q0;
            Q0=makeQuery(id+"F18.imprint","IMPRINT",FACE,{"disambiguationData":[TD([[makeQuery(id+"F18.imprint","IMPRINT",EDGE,{"derivedFrom":sQuery(id+"F18.wireOp",EDGE,"E96")}),1.0]])]});
            var Q1;
            Q1=makeQuery(id+"F18.imprint","IMPRINT",FACE,{"disambiguationData":[TD([[makeQuery(id+"F18.imprint","IMPRINT",EDGE,{"derivedFrom":sQuery(id+"F18.wireOp",EDGE,"E97")}),1.0]])]});
            extrude(context, id + "F19", {"entities" : qUnion([Q0, Q1]), "operationType" : NewBodyOperationType.REMOVE, "endBound" : BoundingType.THROUGH_ALL, "oppositeDirection" : true, "depth" : 25 * mm});
        }
    });
